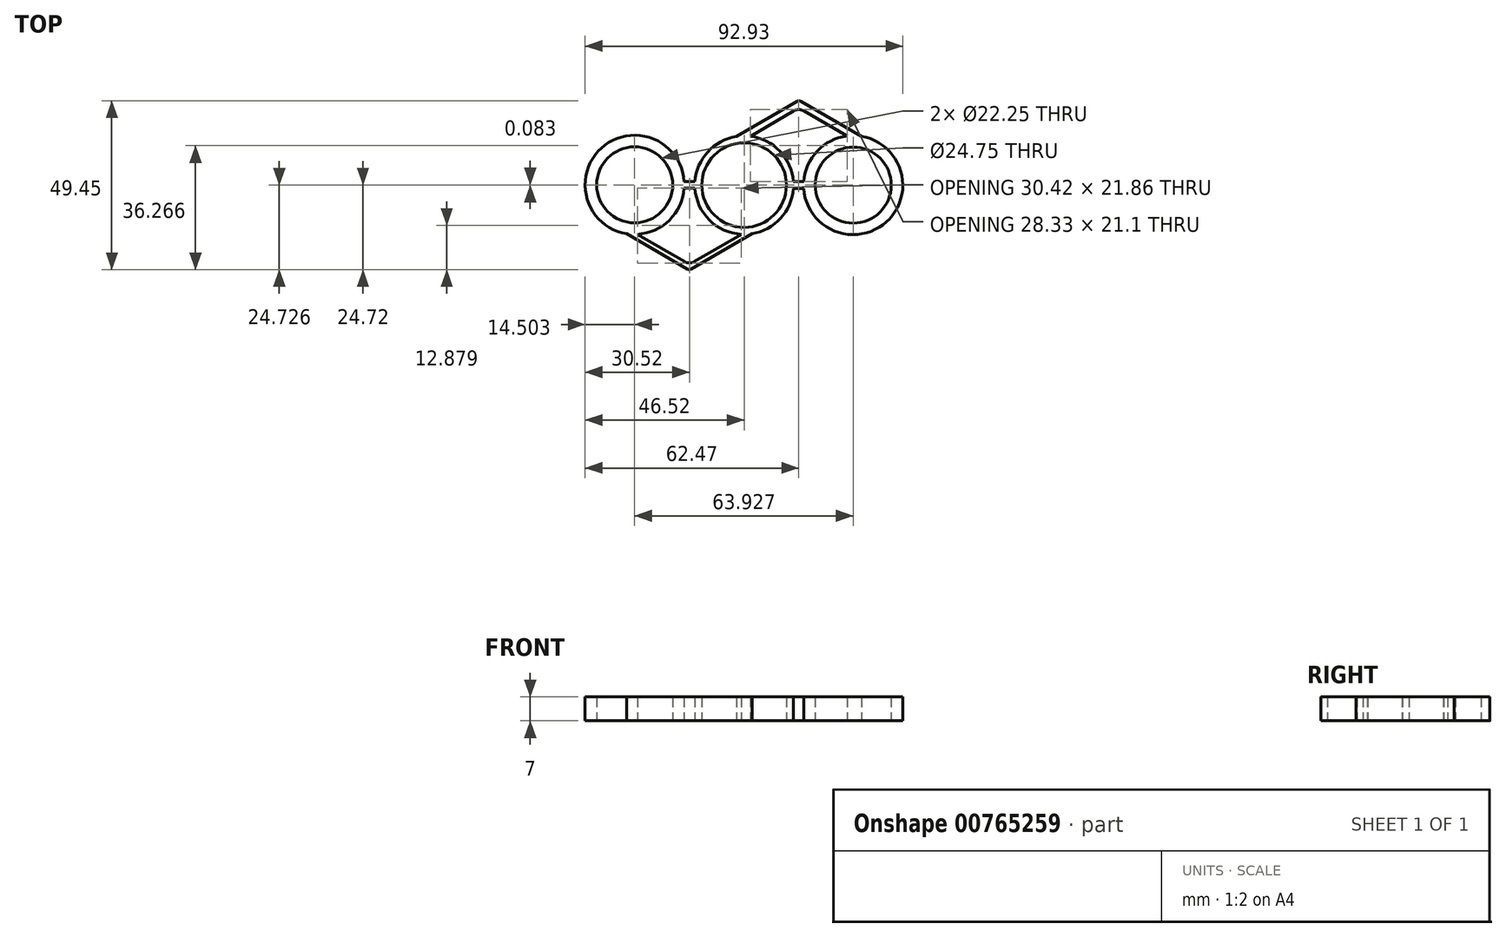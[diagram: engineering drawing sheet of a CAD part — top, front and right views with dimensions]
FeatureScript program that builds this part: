
annotation { "Feature Type Name" : "Feature", "Feature Type Description" : "" }
export const myFeature = defineFeature(function(context is Context, id is Id, definition is map)
    precondition{}
    {
        {
            var Q0;
            Q0=qCreatedBy(makeId("Top.planeOp"),FACE);
            var sketch = newSketch(context, id + "F0", { "sketchPlane" : qUnion([Q0])});
            skCircle(sketch, "E0", {"center": v(0, 0) * mm, "radius": 12.38 * mm});
            skCircle(sketch, "E1", {"center": v(0, 0) * mm, "radius": 14.41 * mm});
            skCircle(sketch, "E2", {"center": v(31.91, 0) * mm, "radius": 11.12 * mm});
            skCircle(sketch, "E3", {"center": v(31.91, 0) * mm, "radius": 14.5 * mm});
            skCircle(sketch, "E4", {"center": v(-32.02, 0.09) * mm, "radius": 11.12 * mm});
            skCircle(sketch, "E5", {"center": v(-32.02, 0.09) * mm, "radius": 14.5 * mm});
            skLineSegment(sketch, "E6", {"start": v(-16.02, -0.91) * mm, "end": v(-17.55, -0.91) * mm});
            skLineSegment(sketch, "E7", {"start": v(-15.91, 1) * mm, "end": v(-14.38, 1) * mm});
            skLineSegment(sketch, "E8", {"start": v(14.38, 1) * mm, "end": v(17.44, 1) * mm});
            skLineSegment(sketch, "E9", {"start": v(17.44, -1) * mm, "end": v(14.38, -1) * mm});
            skLineSegment(sketch, "E10", {"start": v(-24.5, -18.3) * mm, "end": v(-17.5, -22.36) * mm});
            skLineSegment(sketch, "E11", {"start": v(-24.5, -18.3) * mm, "end": v(-31.21, -14.39) * mm});
            skLineSegment(sketch, "E12", {"start": v(-24.52, -19.93) * mm, "end": v(-34.32, -14.23) * mm});
            skLineSegment(sketch, "E13", {"start": v(-24.52, -19.93) * mm, "end": v(-16.52, -24.59) * mm});
            skLineSegment(sketch, "E14", {"start": v(-15.51, -24.59) * mm, "end": v(2.3, -14.23) * mm});
            skLineSegment(sketch, "E15", {"start": v(-14.5, -22.36) * mm, "end": v(-0.79, -14.39) * mm});
            skLineSegment(sketch, "E16", {"start": v(7.51, 19.93) * mm, "end": v(-2.3, 14.23) * mm});
            skLineSegment(sketch, "E17", {"start": v(7.51, 19.93) * mm, "end": v(15.51, 24.59) * mm});
            skLineSegment(sketch, "E18", {"start": v(16.52, 24.6) * mm, "end": v(34.37, 14.3) * mm});
            skLineSegment(sketch, "E19", {"start": v(8.5, 18.2) * mm, "end": v(14.48, 21.7) * mm});
            skLineSegment(sketch, "E20", {"start": v(8.5, 18.2) * mm, "end": v(1.78, 14.3) * mm});
            skLineSegment(sketch, "E21", {"start": v(17.5, 21.7) * mm, "end": v(30.11, 14.4) * mm});
            skPoint(sketch, "E22.visualSharp", {"position": v(16.01, 24.88) * mm});
            skArc(sketch, "E22.filletArc", {"start": v(16.52, 24.6) * mm, "mid": v(16.01, 24.73) * mm, "end": v(15.51, 24.59) * mm});
            skPoint(sketch, "E23.visualSharp", {"position": v(15.99, 22.57) * mm});
            skArc(sketch, "E23.filletArc", {"start": v(17.5, 21.7) * mm, "mid": v(15.99, 22.1) * mm, "end": v(14.48, 21.7) * mm});
            skPoint(sketch, "E24.visualSharp", {"position": v(-16.01, -24.88) * mm});
            skArc(sketch, "E24.filletArc", {"start": v(-16.52, -24.59) * mm, "mid": v(-16.01, -24.72) * mm, "end": v(-15.51, -24.59) * mm});
            skArc(sketch, "E25.filletArc", {"start": v(-17.5, -22.36) * mm, "mid": v(-16, -22.77) * mm, "end": v(-14.5, -22.36) * mm});
            skLineSegment(sketch, "E26", {"start": v(-15.91, 1) * mm, "end": v(-17.54, 1) * mm});
            skLineSegment(sketch, "E27", {"start": v(-16.02, -0.91) * mm, "end": v(-14.38, -0.91) * mm});
            skSolve(sketch);
        }
        {
            var Q0;
            Q0=makeQuery(id+"F0.imprint","IMPRINT",FACE,{"disambiguationData":[TD([[makeQuery(id+"F0.imprint","IMPRINT",EDGE,{"derivedFrom":sQuery(id+"F0.wireOp",EDGE,"E4")}),-1.0]])]});
            var Q1;
            Q1=makeQuery(id+"F0.imprint","IMPRINT",FACE,{"disambiguationData":[TD([[makeQuery(id+"F0.imprint","IMPRINT",EDGE,{"derivedFrom":sQuery(id+"F0.wireOp",EDGE,"E0")}),-1.0]])]});
            var Q2;
            Q2=makeQuery(id+"F0.imprint","IMPRINT",FACE,{"disambiguationData":[TD([[makeQuery(id+"F0.imprint","IMPRINT",EDGE,{"derivedFrom":sQuery(id+"F0.wireOp",EDGE,"E10")}),-1.0]])]});
            var Q3;
            Q3=makeQuery(id+"F0.imprint","IMPRINT",FACE,{"disambiguationData":[TD([[makeQuery(id+"F0.imprint","IMPRINT",EDGE,{"derivedFrom":sQuery(id+"F0.wireOp",EDGE,"E2")}),-1.0]])]});
            var Q4;
            {var subQ0=sQuery(id+"F0.wireOp",EDGE,"E8");Q4=makeQuery(id+"F0.imprint","IMPRINT",FACE,{"disambiguationData":[TD([[makeQuery(id+"F0.imprint","IMPRINT",EDGE,{"derivedFrom":subQ0}),-1.0]])]});}
            var Q5;
            {var subQ4=sQuery(id+"F0.wireOp",EDGE,"E16");Q5=makeQuery(id+"F0.imprint","IMPRINT",FACE,{"disambiguationData":[TD([[makeQuery(id+"F0.imprint","IMPRINT",EDGE,{"derivedFrom":subQ4}),1.0]])]});}
            var Q6;
            {var subQ1=sQuery(id+"F0.wireOp",EDGE,"E6");Q6=makeQuery(id+"F0.imprint","IMPRINT",FACE,{"disambiguationData":[TD([[makeQuery(id+"F0.imprint","IMPRINT",EDGE,{"derivedFrom":subQ1}),-1.0]])]});}
            extrude(context, id + "F1", {"entities" : qUnion([Q0, Q1, Q2, Q3, Q4, Q5, Q6]), "depth" : 7 * mm, "offsetDistance" : 25 * mm});
        }
    });
